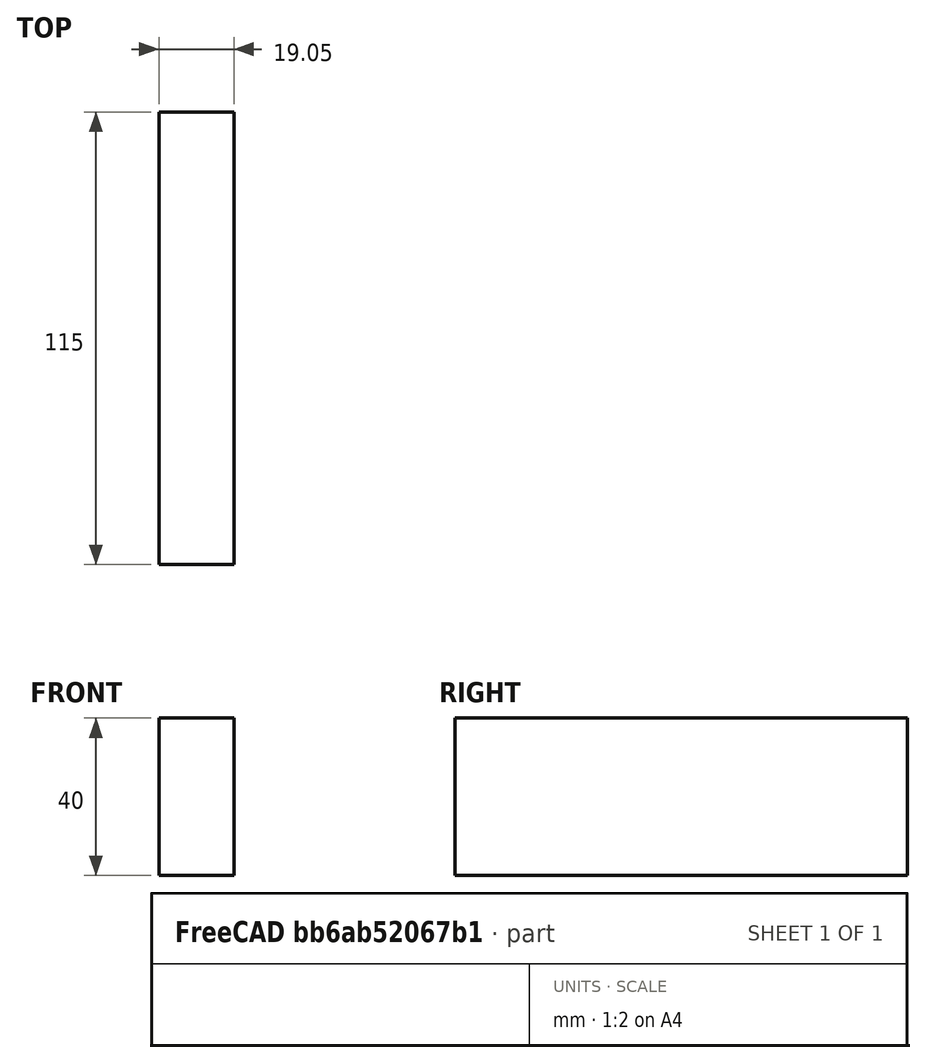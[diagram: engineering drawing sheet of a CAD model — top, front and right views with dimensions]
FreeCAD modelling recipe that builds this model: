
FCSTD DOCUMENT  (FreeCAD 0.19R24291 (Git))
Label: side
License: All rights reserved
LicenseURL: http://en.wikipedia.org/wiki/All_rights_reserved
objects: TechDraw::DrawViewDimension×2, Sketcher::SketchObject×1, PartDesign::Pad×1, PartDesign::Body×1, TechDraw::DrawSVGTemplate×1, TechDraw::DrawViewPart×1, TechDraw::DrawPage×1
note: 4 computed .brp shape members not serialized (recipe doc carries the construction recipe); baked Part::Feature solids carry a one-line shape summary decoded from their .brp

FEATURE [Sketcher::SketchObject] Sketch
  FullyConstrained = true
  MapMode = 5
  Placement = pos=(0,0,0) rot=(0.57735,0.57735,0.57735;2.0944rad)
  Support = -> [YZ_Plane]
  sketch-geometry (4):
    g0: LineSegment StartX=0 StartY=0 StartZ=0 EndX=115 EndY=0 EndZ=0
    g1: LineSegment StartX=115 StartY=0 StartZ=0 EndX=115 EndY=40 EndZ=0
    g2: LineSegment StartX=115 StartY=40 StartZ=0 EndX=0 EndY=40 EndZ=0
    g3: LineSegment StartX=0 StartY=40 StartZ=0 EndX=0 EndY=0 EndZ=0
  constraints (11):
    c: Coincident(g0,g1)
    c: Coincident(g1,g2)
    c: Coincident(g2,g3)
    c: Coincident(g3,g0)
    c: Horizontal(g0)
    c: Horizontal(g2)
    c: Vertical(g1)
    c: Vertical(g3)
    c: Coincident(g0,g-1)
    c: DistanceX(g0,g0) = 115
    c: DistanceY(g3,g3) = 40
FEATURE [PartDesign::Pad] Pad
  Direction = (1,1,1)
  Length = 19.05
  Length2 = 100
  Placement = pos=(0,0,0) rot=(0.57735,0.57735,0.57735;2.0944rad)
  Profile = -> Sketch
  Type = 0
  expr: Length = 3 / 4 * 25.4
FEATURE [PartDesign::Body] Body
  Group = -> [Sketch,Pad]
  Origin = -> Origin
  Tip = -> Pad
FEATURE [TechDraw::DrawSVGTemplate] Template
  EditableTexts = Designed_by_Name=Designed by Name; Drawing_number=Drawing number; FC-Date=Date; FC-SC=Scale; FC-SH=Sheet; FC-Title=Title; Subtitle=Subtitle; Weight=Weight
  Height = 210
  Orientation = 1
  Width = 297
FEATURE [TechDraw::DrawViewPart] View
  CoarseView = false
  Direction = (1,0,0)
  Focus = 100
  HardHidden = false
  IsoCount = 0
  IsoHidden = false
  IsoVisible = false
  LockPosition = false
  Perspective = false
  Rotation = 0
  ScaleType = 0
  SeamHidden = false
  SeamVisible = true
  SmoothHidden = false
  SmoothVisible = true
  Source = -> [Body]
  X = 148.5
  XDirection = (0,1,0)
  Y = 105
FEATURE [TechDraw::DrawViewDimension] Dimension
  Arbitrary = false
  ArbitraryTolerances = false
  EqualTolerance = true
  FormatSpec = %.2f
  FormatSpecOverTolerance = %+.2f
  FormatSpecUnderTolerance = %+.2f
  Inverted = false
  LockPosition = false
  MeasureType = 1
  OverTolerance = 0
  References2D = -> [View]
  Rotation = 0
  ScaleType = 0
  TheoreticalExact = false
  Type = 2
  UnderTolerance = 0
  X = -77.4286
  Y = 1.28571
FEATURE [TechDraw::DrawViewDimension] Dimension001
  Arbitrary = false
  ArbitraryTolerances = false
  EqualTolerance = true
  FormatSpec = %.2f
  FormatSpecOverTolerance = %+.2f
  FormatSpecUnderTolerance = %+.2f
  Inverted = false
  LockPosition = false
  MeasureType = 1
  OverTolerance = 0
  References2D = -> [View]
  Rotation = 0
  ScaleType = 0
  TheoreticalExact = false
  Type = 1
  UnderTolerance = 0
  X = -2.57143
  Y = 41.6429
FEATURE [TechDraw::DrawPage] Page
  KeepUpdated = true
  NextBalloonIndex = 1
  ProjectionType = 0
  Template = -> Template
  Views = -> [View,Dimension,Dimension001]
